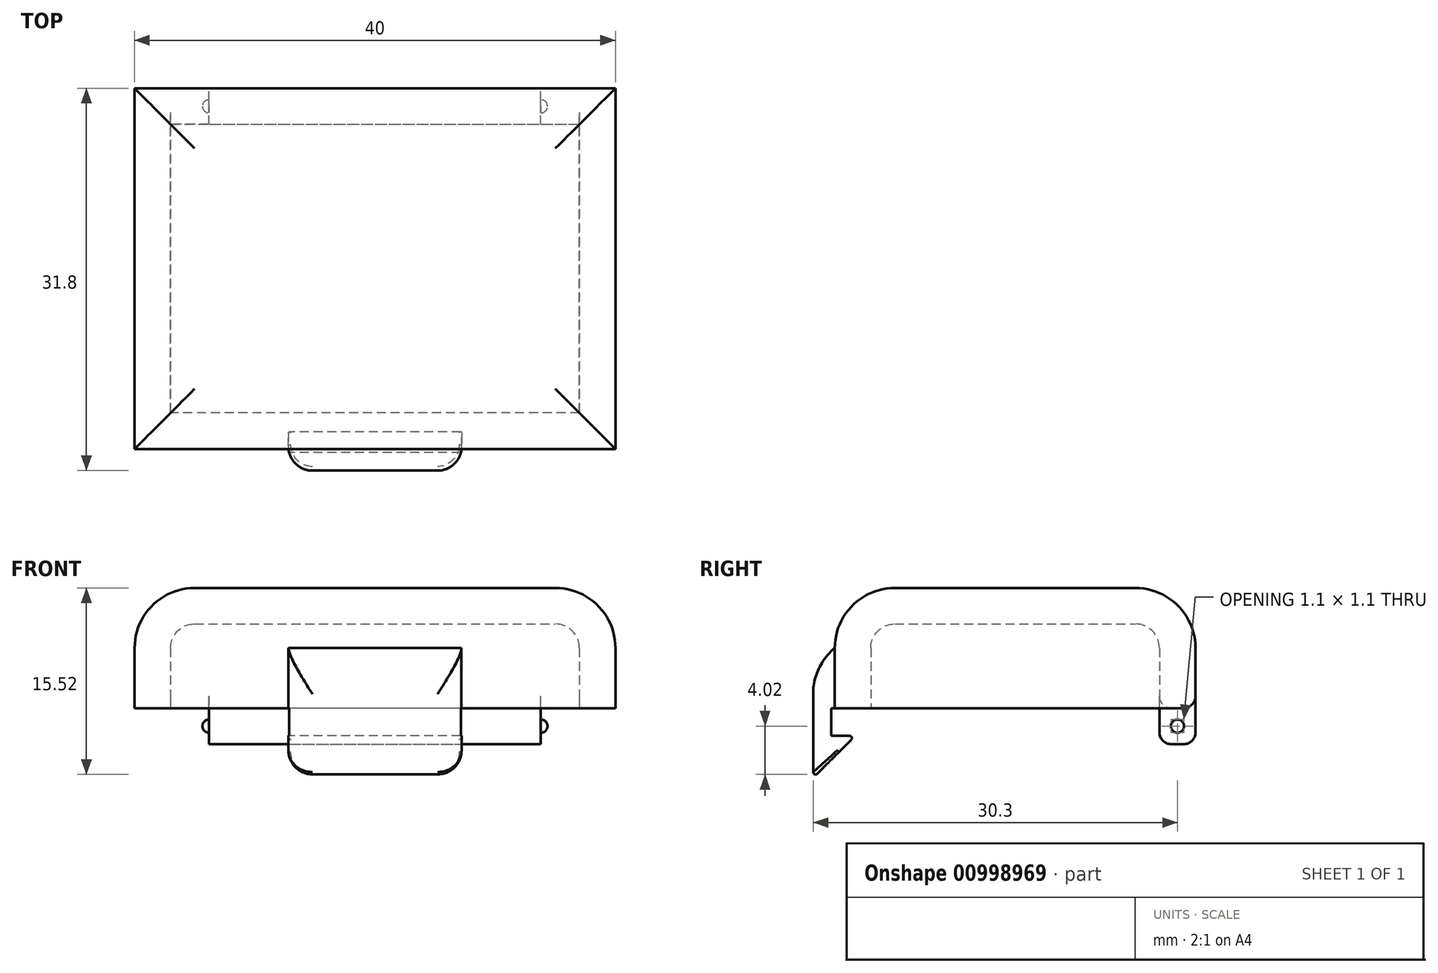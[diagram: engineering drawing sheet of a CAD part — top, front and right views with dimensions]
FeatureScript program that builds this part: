
annotation { "Feature Type Name" : "Feature", "Feature Type Description" : "" }
export const myFeature = defineFeature(function(context is Context, id is Id, definition is map)
    precondition{}
    {
        {
            var Q0;
            Q0=qCreatedBy(makeId("Top.planeOp"),FACE);
            var sketch = newSketch(context, id + "F0", { "sketchPlane" : qUnion([Q0])});
            skLineSegment(sketch, "E0.bottom", {"start": v(20, 15) * mm, "end": v(-20, 15) * mm});
            skLineSegment(sketch, "E0.top", {"start": v(20, -15) * mm, "end": v(-20, -15) * mm});
            skLineSegment(sketch, "E0.left", {"start": v(20, 15) * mm, "end": v(20, -15) * mm});
            skLineSegment(sketch, "E0.right", {"start": v(-20, 15) * mm, "end": v(-20, -15) * mm});
            skPoint(sketch, "E0.middle", {"position": v(0, 0) * mm});
            skSolve(sketch);
        }
        {
            var Q0;
            Q0=qSketchRegion(id+"F0",true);
            extrude(context, id + "F1", {"entities" : qUnion([Q0]), "depth" : 10 * mm, "offsetDistance" : 25 * mm});
        }
        {
            var Q0;
            Q0=makeQuery(id+"F1.opExtrude","CAP_FACE",FACE,{"disambiguationData":[OSD([sQuery(id+"F0.wireOp",EDGE,"E0.bottom"),sQuery(id+"F0.wireOp",EDGE,"E0.top"),sQuery(id+"F0.wireOp",EDGE,"E0.left"),sQuery(id+"F0.wireOp",EDGE,"E0.right")])],"isStart":false});
            fillet(context, id + "F2", {"entities" : qUnion([Q0]), "radius" : 5 * mm, "tangentPropagation" : true, "allowEdgeOverflow" : false});
        }
        {
            var Q0;
            Q0=makeQuery(id+"F1.opExtrude","CAP_FACE",FACE,{"disambiguationData":[OSD([sQuery(id+"F0.wireOp",EDGE,"E0.bottom"),sQuery(id+"F0.wireOp",EDGE,"E0.top"),sQuery(id+"F0.wireOp",EDGE,"E0.left"),sQuery(id+"F0.wireOp",EDGE,"E0.right")])],"isStart":true});
            shell(context, id + "F3", {"entities" : qUnion([Q0]), "thickness" : 3 * mm});
        }
        {
            var Q0;
            Q0=qCreatedBy(makeId("Top.planeOp"),FACE);
            var sketch = newSketch(context, id + "F4", { "sketchPlane" : qUnion([Q0])});
            skLineSegment(sketch, "E1.0", {"start": v(17, 12) * mm, "end": v(-17, 12) * mm, "construction": true});
            skLineSegment(sketch, "E2.0", {"start": v(20, 15) * mm, "end": v(-20, 15) * mm, "construction": true});
            skPoint(sketch, "E3.0", {"position": v(0, 0) * mm});
            skLineSegment(sketch, "E4.bottom", {"start": v(-13.8, 12) * mm, "end": v(13.8, 12) * mm});
            skLineSegment(sketch, "E4.top", {"start": v(-13.8, 15) * mm, "end": v(13.8, 15) * mm});
            skLineSegment(sketch, "E4.left", {"start": v(-13.8, 12) * mm, "end": v(-13.8, 15) * mm});
            skLineSegment(sketch, "E4.right", {"start": v(13.8, 12) * mm, "end": v(13.8, 15) * mm});
            skPoint(sketch, "E5", {"position": v(0, 12) * mm});
            skSolve(sketch);
        }
        {
            var Q0;
            Q0=qSketchRegion(id+"F4",true);
            extrude(context, id + "F5", {"entities" : qUnion([Q0]), "operationType" : NewBodyOperationType.ADD, "oppositeDirection" : true, "depth" : 3 * mm, "offsetDistance" : 25 * mm});
        }
        {
            var Q0;
            Q0=qCreatedBy(makeId("Top.planeOp"),FACE);
            var sketch = newSketch(context, id + "F6", { "sketchPlane" : qUnion([Q0])});
            skLineSegment(sketch, "E6.bottom", {"start": v(0, 25.94) * mm, "end": v(46.03, 25.94) * mm});
            skLineSegment(sketch, "E6.top", {"start": v(0, -43.63) * mm, "end": v(46.03, -43.63) * mm});
            skLineSegment(sketch, "E6.left", {"start": v(0, 25.94) * mm, "end": v(0, -43.63) * mm});
            skLineSegment(sketch, "E6.right", {"start": v(46.03, 25.94) * mm, "end": v(46.03, -43.63) * mm});
            skSolve(sketch);
        }
        {
            var Q0;
            Q0=makeQuery(id+"F6.imprint","IMPRINT",FACE,{"disambiguationData":[TD([[makeQuery(id+"F6.imprint","IMPRINT",EDGE,{"derivedFrom":sQuery(id+"F6.wireOp",EDGE,"E6.bottom")}),-1.0]])]});
            extrude(context, id + "F7", {"entities" : qUnion([Q0]), "operationType" : NewBodyOperationType.REMOVE, "endBound" : BoundingType.SYMMETRIC, "depth" : 25 * mm, "offsetDistance" : 25 * mm});
        }
        {
            var Q0;
            Q0=makeQuery(id+"F5.opExtrude","SWEPT_FACE",FACE,{"disambiguationData":[OSD([sQuery(id+"F4.wireOp",EDGE,"E4.left")])]});
            var sketch = newSketch(context, id + "F8", { "sketchPlane" : qUnion([Q0])});
            skLineSegment(sketch, "E7.0", {"start": v(-12, 0) * mm, "end": v(-15, 0) * mm, "construction": true});
            skLineSegment(sketch, "E8.0", {"start": v(-12, -3) * mm, "end": v(-12, 0) * mm, "construction": true});
            skPoint(sketch, "E9", {"position": v(-13.5, 0) * mm});
            skPoint(sketch, "E10", {"position": v(-12, -1.5) * mm});
            skCircle(sketch, "E11", {"center": v(-13.5, -1.5) * mm, "radius": 0.55 * mm});
            skSolve(sketch);
        }
        {
            var Q0;
            Q0=qSketchRegion(id+"F8",true);
            extrude(context, id + "F9", {"entities" : qUnion([Q0]), "operationType" : NewBodyOperationType.ADD, "depth" : .55 * mm, "offsetDistance" : 25 * mm});
        }
        {
            var Q0;
            Q0=makeQuery(id+"F9.opExtrude","CAP_EDGE",EDGE,{"disambiguationData":[OSD([sQuery(id+"F8.wireOp",EDGE,"E11")])],"isStart":false});
            fillet(context, id + "F10", {"entities" : qUnion([Q0]), "radius" : .55 * mm, "tangentPropagation" : true, "allowEdgeOverflow" : false});
        }
        {
            var Q0;
            Q0=makeQuery(id+"F5.opExtrude","CAP_EDGE",EDGE,{"disambiguationData":[OSD([sQuery(id+"F4.wireOp",EDGE,"E4.top")])],"isStart":false});
            var Q1;
            Q1=makeQuery(id+"F5.opExtrude","CAP_EDGE",EDGE,{"disambiguationData":[OSD([sQuery(id+"F4.wireOp",EDGE,"E4.bottom")])],"isStart":false});
            var Q2;
            {var subQ0=sQuery(id+"F0.wireOp",EDGE,"E0.right");var subQ1=sQuery(id+"F0.wireOp",EDGE,"E0.bottom");Q2=makeQuery(id+"F5.boolean.opBoolean","SPLIT",EDGE,{"disambiguationData":[TD([makeQuery(id+"F1.opExtrude","SWEPT_FACE",FACE,{"disambiguationData":[OSD([subQ0])]})])],"derivedFrom":makeQuery(id+"F1.opExtrude","CAP_EDGE",EDGE,{"disambiguationData":[OSD([subQ1])],"isStart":true})});}
            var Q3;
            {var subQ1=sQuery(id+"F0.wireOp",EDGE,"E0.bottom");Q3=makeQuery(id+"F5.boolean.opBoolean","SPLIT",EDGE,{"disambiguationData":[TD([makeQuery(id+"F5.opExtrude","SWEPT_FACE",FACE,{"disambiguationData":[OSD([sQuery(id+"F4.wireOp",EDGE,"E4.left")])]})])],"derivedFrom":makeQuery(id+"F3.opShell","OFFSET_EDGE",EDGE,{"disambiguationData":[OSD([subQ1]),TDD([makeQuery(id+"F1.opExtrude","CAP_EDGE",EDGE,{"disambiguationData":[OSD([subQ1])],"isStart":true})])]})});}
            fillet(context, id + "F11", {"entities" : qUnion([Q0, Q1, Q2, Q3]), "radius" : 1 * mm, "tangentPropagation" : true, "allowEdgeOverflow" : false});
        }
        {
            var Q0;
            Q0=makeQuery(id+"F1.opExtrude","SWEPT_BODY",BODY,{"disambiguationData":[OSD([sQuery(id+"F0.wireOp",EDGE,"E0.bottom"),sQuery(id+"F0.wireOp",EDGE,"E0.top"),sQuery(id+"F0.wireOp",EDGE,"E0.left"),sQuery(id+"F0.wireOp",EDGE,"E0.right")])]});
            var Q1;
            Q1=qCreatedBy(makeId("Right.planeOp"),FACE);
            mirror(context, id + "F12", {"operationType" : NewBodyOperationType.ADD, "entities" : qUnion([Q0]), "mirrorPlane" : qUnion([Q1])});
        }
        {
            var Q0;
            {var subQ0=makeQuery(id+"F1.opExtrude","SWEPT_FACE",FACE,{"disambiguationData":[OSD([sQuery(id+"F0.wireOp",EDGE,"E0.top")])]});Q0=makeQuery(id+"F12.boolean.opBoolean","MERGE",FACE,{"derivedFrom":[subQ0,makeQuery(id+"F12.opPattern","COPY",FACE,{"derivedFrom":subQ0,"instanceName":"1"})]});}
            var sketch = newSketch(context, id + "F13", { "sketchPlane" : qUnion([Q0])});
            skLineSegment(sketch, "E12.bottom", {"start": v(7.2, 5) * mm, "end": v(-7.2, 5) * mm});
            skLineSegment(sketch, "E12.top", {"start": v(7.2, -7) * mm, "end": v(-7.2, -7) * mm});
            skLineSegment(sketch, "E12.left", {"start": v(7.2, 5) * mm, "end": v(7.2, -7) * mm});
            skLineSegment(sketch, "E12.right", {"start": v(-7.2, 5) * mm, "end": v(-7.2, -7) * mm});
            skPoint(sketch, "E12.middle", {"position": v(0, -1) * mm});
            skSolve(sketch);
        }
        {
            var Q0;
            Q0=qSketchRegion(id+"F13",true);
            extrude(context, id + "F14", {"entities" : qUnion([Q0]), "operationType" : NewBodyOperationType.ADD, "endBound" : BoundingType.SYMMETRIC, "depth" : 3.6 * mm, "offsetDistance" : 25 * mm});
        }
        {
            var Q0;
            Q0=makeQuery(id+"F14.opExtrude","SWEPT_FACE",FACE,{"disambiguationData":[OSD([sQuery(id+"F13.wireOp",EDGE,"E12.right")])]});
            var sketch = newSketch(context, id + "F15", { "sketchPlane" : qUnion([Q0])});
            skLineSegment(sketch, "E13", {"start": v(15, 0) * mm, "end": v(15.3, 0) * mm});
            skLineSegment(sketch, "E14", {"start": v(15.3, 0) * mm, "end": v(15.3, -2.3) * mm});
            skLineSegment(sketch, "E15", {"start": v(15.3, -2.3) * mm, "end": v(13.3, -2.3) * mm});
            skLineSegment(sketch, "E16", {"start": v(13.3, -2.3) * mm, "end": v(16.8, -5.8) * mm});
            skLineSegment(sketch, "E17", {"start": v(16.8, -5.8) * mm, "end": v(16.8, -7) * mm});
            skLineSegment(sketch, "E18", {"start": v(16.8, -7) * mm, "end": v(13.2, -7) * mm});
            skLineSegment(sketch, "E19", {"start": v(13.2, -7) * mm, "end": v(13.2, 0) * mm});
            skLineSegment(sketch, "E20", {"start": v(13.2, 0) * mm, "end": v(15, 0) * mm});
            skSolve(sketch);
        }
        {
            var Q0;
            Q0=qSketchRegion(id+"F15",true);
            extrude(context, id + "F16", {"entities" : qUnion([Q0]), "operationType" : NewBodyOperationType.REMOVE, "oppositeDirection" : true, "depth" : 25 * mm, "offsetDistance" : 25 * mm});
        }
        {
            var Q0;
            Q0=makeQuery(id+"F14.opExtrude","CAP_EDGE",EDGE,{"disambiguationData":[OSD([sQuery(id+"F13.wireOp",EDGE,"E12.right")])],"isStart":false});
            var Q1;
            Q1=makeQuery(id+"F14.opExtrude","CAP_EDGE",EDGE,{"disambiguationData":[OSD([sQuery(id+"F13.wireOp",EDGE,"E12.left")])],"isStart":false});
            fillet(context, id + "F17", {"entities" : qUnion([Q0, Q1]), "radius" : 2 * mm, "tangentPropagation" : true, "allowEdgeOverflow" : false});
        }
        {
            var Q0;
            Q0=makeQuery(id+"F14.opExtrude","CAP_EDGE",EDGE,{"disambiguationData":[OSD([sQuery(id+"F13.wireOp",EDGE,"E12.bottom")])],"isStart":false});
            fillet(context, id + "F18", {"entities" : qUnion([Q0]), "radius" : 5 * mm, "tangentPropagation" : true, "allowEdgeOverflow" : false});
        }
        {
            var Q0;
            Q0=makeQuery(id+"F16.boolean.opBoolean","COPY",FACE,{"derivedFrom":makeQuery(id+"F16.opExtrude","SWEPT_FACE",FACE,{"disambiguationData":[OSD([sQuery(id+"F15.wireOp",EDGE,"E16")])]})});
            fillet(context, id + "F19", {"entities" : qUnion([Q0]), "radius" : .2 * mm, "tangentPropagation" : true, "allowEdgeOverflow" : false});
        }
    });
